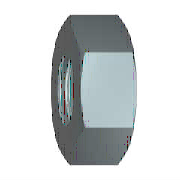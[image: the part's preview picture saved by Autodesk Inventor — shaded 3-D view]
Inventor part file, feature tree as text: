
AUTODESK INVENTOR PART (.ipt)
format: ipt  version: 2024 (Build 280153000, 153)  size: 172,032 bytes
history: native  units: mm (DEFAULTED — no unit token found)
features: chamfer x1, hole x1, other x1, plane x1
ambient origin geometry x7: Origin, YZ Plane, XZ Plane, X Axis, Y Axis, Z Axis, Center Point
bodies: Solid1 (feature_tree), Body (feature_tree)
feature tree (4):
  chamfer  "Chamfer1"  Distance=8.082904mm
  hole  "Thread"  [1 undecoded]
  other  "Work Axis1"
  plane  "Work Plane1"
note: 1 required parameter value undecoded (feature->parameter linkage not recoverable at this tier; creation-order binding heuristic only, values carry confidence <= 0.55)
